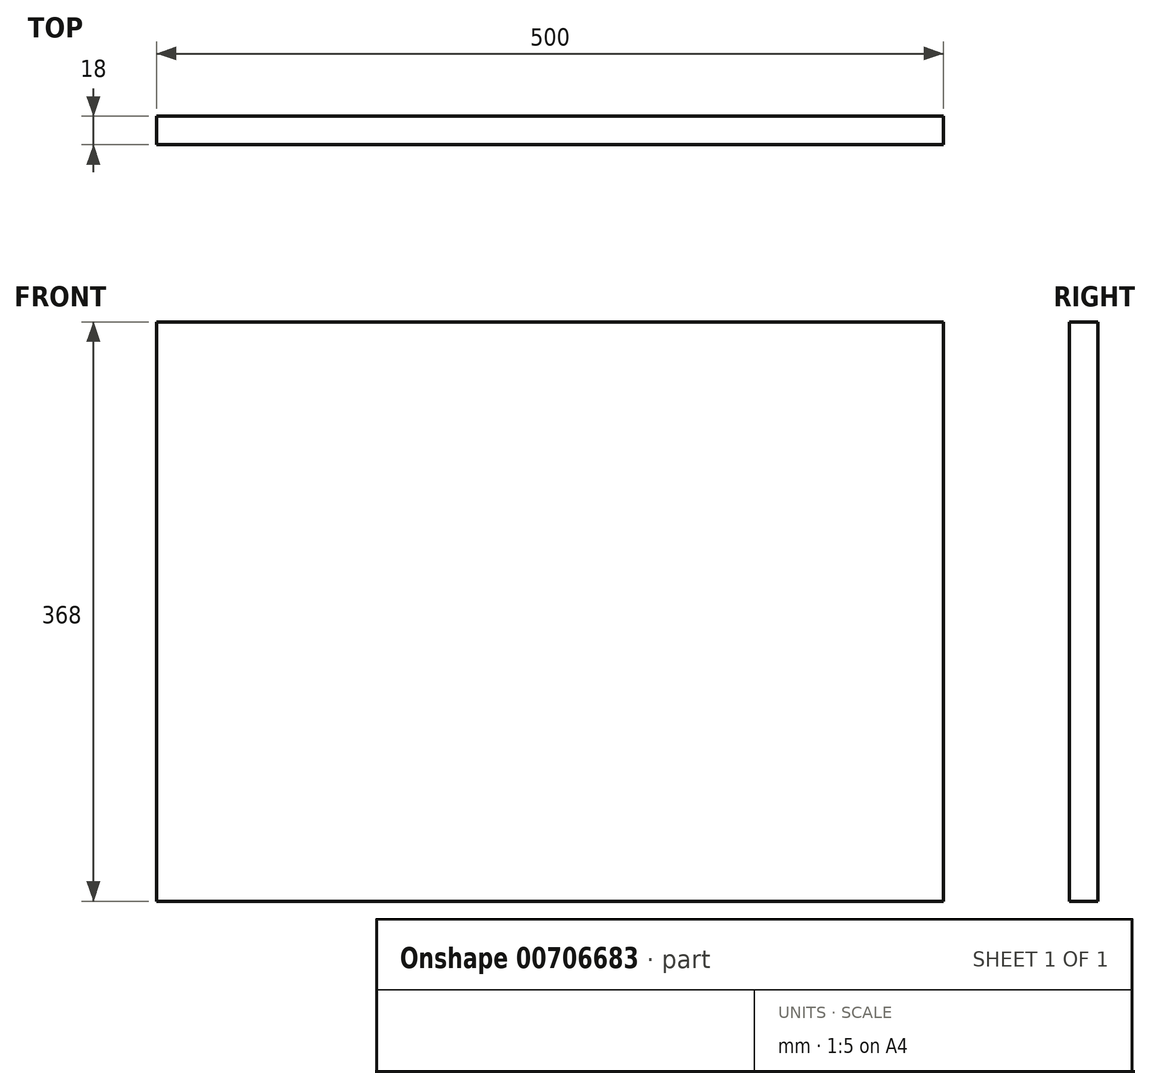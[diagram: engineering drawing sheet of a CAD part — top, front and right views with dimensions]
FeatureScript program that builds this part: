
annotation { "Feature Type Name" : "Feature", "Feature Type Description" : "" }
export const myFeature = defineFeature(function(context is Context, id is Id, definition is map)
    precondition{}
    {
        {
            var Q0;
            Q0=qCreatedBy(makeId("Front.planeOp"),FACE);
            var sketch = newSketch(context, id + "F0", { "sketchPlane" : qUnion([Q0])});
            skLineSegment(sketch, "E0.bottom", {"start": v(-250, -184) * mm, "end": v(250, -184) * mm});
            skLineSegment(sketch, "E0.top", {"start": v(-250, 184) * mm, "end": v(250, 184) * mm});
            skLineSegment(sketch, "E0.left", {"start": v(-250, -184) * mm, "end": v(-250, 184) * mm});
            skLineSegment(sketch, "E0.right", {"start": v(250, -184) * mm, "end": v(250, 184) * mm});
            skPoint(sketch, "E0.middle", {"position": v(0, 0) * mm});
            skSolve(sketch);
        }
        {
            var Q0;
            Q0=makeQuery(id+"F0.imprint","IMPRINT",FACE,{"disambiguationData":[TD([[makeQuery(id+"F0.imprint","IMPRINT",EDGE,{"derivedFrom":sQuery(id+"F0.wireOp",EDGE,"E0.bottom")}),1.0]])]});
            extrude(context, id + "F1", {"entities" : qUnion([Q0]), "depth" : 18 * mm, "offsetDistance" : 25 * mm, "symmetric" : true});
        }
    });
